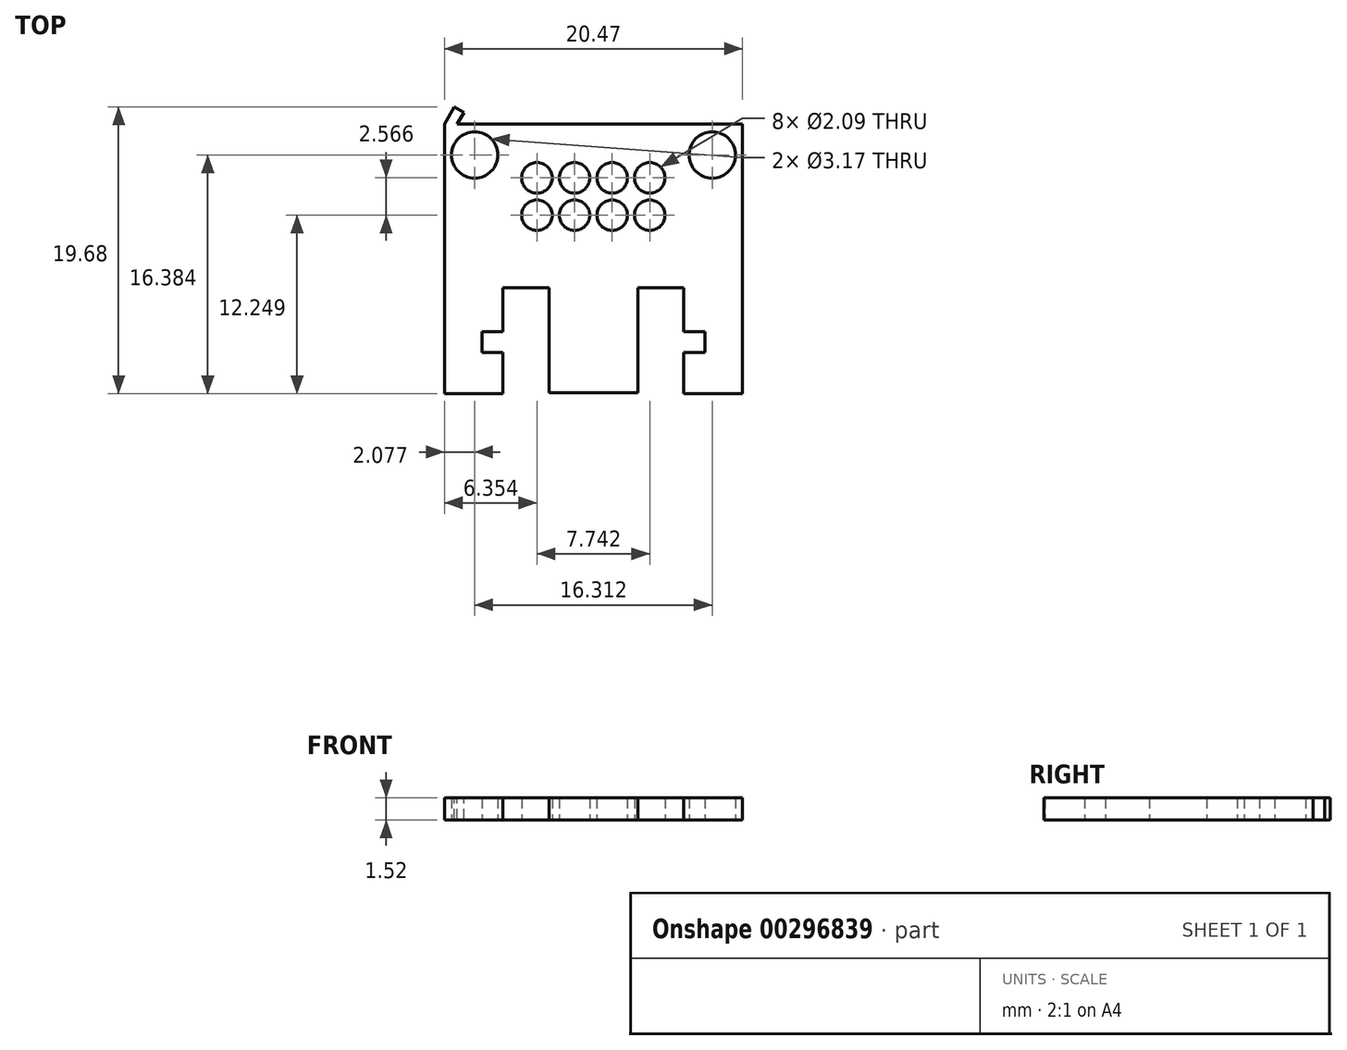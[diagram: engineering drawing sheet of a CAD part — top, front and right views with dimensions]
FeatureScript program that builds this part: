
annotation { "Feature Type Name" : "Feature", "Feature Type Description" : "" }
export const myFeature = defineFeature(function(context is Context, id is Id, definition is map)
    precondition{}
    {
        {
            var Q0;
            Q0=qCreatedBy(makeId("Top.planeOp"),FACE);
            var sketch = newSketch(context, id + "F0", { "sketchPlane" : qUnion([Q0])});
            skLineSegment(sketch, "E0.bottom", {"start": v(2.07, -0.14) * mm, "end": v(12.3, -0.14) * mm});
            skLineSegment(sketch, "E0.top", {"start": v(2.07, -18.64) * mm, "end": v(6.1, -18.64) * mm});
            skLineSegment(sketch, "E0.left", {"start": v(2.07, -0.14) * mm, "end": v(2.07, -18.64) * mm});
            skLineSegment(sketch, "E1", {"start": v(6.1, -18.64) * mm, "end": v(6.1, -15.83) * mm});
            skLineSegment(sketch, "E2", {"start": v(6.1, -15.83) * mm, "end": v(4.65, -15.83) * mm});
            skLineSegment(sketch, "E3", {"start": v(4.65, -15.83) * mm, "end": v(4.65, -14.4) * mm});
            skLineSegment(sketch, "E4", {"start": v(4.65, -14.4) * mm, "end": v(6.1, -14.4) * mm});
            skLineSegment(sketch, "E5", {"start": v(6.1, -14.4) * mm, "end": v(6.1, -11.39) * mm});
            skLineSegment(sketch, "E6", {"start": v(6.1, -11.39) * mm, "end": v(9.25, -11.39) * mm});
            skLineSegment(sketch, "E7", {"start": v(9.25, -11.39) * mm, "end": v(9.25, -18.58) * mm});
            skLineSegment(sketch, "E8", {"start": v(9.25, -18.58) * mm, "end": v(12.3, -18.58) * mm});
            skLineSegment(sketch, "E9", {"start": v(12.3, 0) * mm, "end": v(12.3, -18.58) * mm});
            skPoint(sketch, "E10.orphan", {"position": v(15.35, -18.58) * mm});
            skCircle(sketch, "E11", {"center": v(4.15, -2.26) * mm, "radius": 1.59 * mm});
            skSolve(sketch);
        }
        {
            var Q0;
            {var subQ0=sQuery(id+"F0.wireOp",EDGE,"E0.bottom");Q0=makeQuery(id+"F0.imprint","IMPRINT",FACE,{"disambiguationData":[TD([[makeQuery(id+"F0.imprint","IMPRINT",EDGE,{"derivedFrom":subQ0}),-1.0]])]});}
            extrude(context, id + "F1", {"entities" : qUnion([Q0]), "depth" : 1.52 * mm});
        }
        {
            var Q0;
            Q0=makeQuery(id+"F1.opExtrude","SWEPT_BODY",BODY,{"disambiguationData":[OSD([sQuery(id+"F0.wireOp",EDGE,"E0.bottom"),sQuery(id+"F0.wireOp",EDGE,"E0.top"),sQuery(id+"F0.wireOp",EDGE,"E0.left"),sQuery(id+"F0.wireOp",EDGE,"E1"),sQuery(id+"F0.wireOp",EDGE,"E2"),sQuery(id+"F0.wireOp",EDGE,"E3"),sQuery(id+"F0.wireOp",EDGE,"E4"),sQuery(id+"F0.wireOp",EDGE,"E5"),sQuery(id+"F0.wireOp",EDGE,"E6"),sQuery(id+"F0.wireOp",EDGE,"E7"),sQuery(id+"F0.wireOp",EDGE,"E8"),sQuery(id+"F0.wireOp",EDGE,"E9"),sQuery(id+"F0.wireOp",EDGE,"E11")])]});
            var Q1;
            Q1=makeQuery(id+"F1.opExtrude","SWEPT_FACE",FACE,{"disambiguationData":[OSD([sQuery(id+"F0.wireOp",EDGE,"E9")])]});
            mirror(context, id + "F2", {"operationType" : NewBodyOperationType.ADD, "entities" : qUnion([Q0]), "mirrorPlane" : qUnion([Q1])});
        }
        {
            var Q0;
            {var subQ0=makeQuery(id+"F1.opExtrude","CAP_FACE",FACE,{"disambiguationData":[OSD([sQuery(id+"F0.wireOp",EDGE,"E0.bottom"),sQuery(id+"F0.wireOp",EDGE,"E0.top"),sQuery(id+"F0.wireOp",EDGE,"E0.left"),sQuery(id+"F0.wireOp",EDGE,"E1"),sQuery(id+"F0.wireOp",EDGE,"E2"),sQuery(id+"F0.wireOp",EDGE,"E3"),sQuery(id+"F0.wireOp",EDGE,"E4"),sQuery(id+"F0.wireOp",EDGE,"E5"),sQuery(id+"F0.wireOp",EDGE,"E6"),sQuery(id+"F0.wireOp",EDGE,"E7"),sQuery(id+"F0.wireOp",EDGE,"E8"),sQuery(id+"F0.wireOp",EDGE,"E9"),sQuery(id+"F0.wireOp",EDGE,"E11")])],"isStart":true});Q0=makeQuery(id+"F2.boolean.opBoolean","MERGE",FACE,{"derivedFrom":[subQ0,makeQuery(id+"F2.opPattern","COPY",FACE,{"derivedFrom":subQ0,"instanceName":"1"})]});}
            var sketch = newSketch(context, id + "F3", { "sketchPlane" : qUnion([Q0])});
            skCircle(sketch, "E12", {"center": v(16.17, 3.82) * mm, "radius": 1.05 * mm});
            skLineSegment(sketch, "E13.bottom", {"start": v(16.17, 3.82) * mm, "end": v(8.42, 3.82) * mm, "construction": true});
            skLineSegment(sketch, "E13.top", {"start": v(16.17, 6.4) * mm, "end": v(8.42, 6.4) * mm, "construction": true});
            skLineSegment(sketch, "E13.left", {"start": v(16.17, 3.82) * mm, "end": v(16.17, 6.4) * mm, "construction": true});
            skLineSegment(sketch, "E13.right", {"start": v(8.42, 3.82) * mm, "end": v(8.42, 6.4) * mm, "construction": true});
            skCircle(sketch, "E14", {"center": v(13.58, 3.82) * mm, "radius": 1.05 * mm});
            skCircle(sketch, "E15", {"center": v(8.42, 3.82) * mm, "radius": 1.05 * mm});
            skCircle(sketch, "E16", {"center": v(8.42, 6.4) * mm, "radius": 1.05 * mm});
            skCircle(sketch, "E17", {"center": v(13.58, 6.4) * mm, "radius": 1.05 * mm});
            skCircle(sketch, "E18", {"center": v(16.17, 6.4) * mm, "radius": 1.05 * mm});
            skCircle(sketch, "E19", {"center": v(11, 3.82) * mm, "radius": 1.05 * mm});
            skCircle(sketch, "E20", {"center": v(11, 6.4) * mm, "radius": 1.05 * mm});
            skLineSegment(sketch, "E21", {"start": v(16.17, 3.82) * mm, "end": v(13.58, 3.82) * mm, "construction": true});
            skLineSegment(sketch, "E22", {"start": v(13.58, 3.82) * mm, "end": v(11, 3.82) * mm, "construction": true});
            skLineSegment(sketch, "E23", {"start": v(11, 3.82) * mm, "end": v(8.42, 3.82) * mm, "construction": true});
            skLineSegment(sketch, "E24", {"start": v(13.58, 3.82) * mm, "end": v(13.58, 6.4) * mm});
            skLineSegment(sketch, "E25", {"start": v(11, 3.82) * mm, "end": v(11, 6.4) * mm});
            skSolve(sketch);
        }
        {
            var Q0;
            Q0 = qSketchRegion(id + "F3", true);
            var Q1;
            Q1 = qConstructionFilter(qBodyType(qCreatedBy(id + "F3" ,EDGE), BodyType.WIRE), ConstructionObject.NO);
            extrude(context, id + "F4", {"entities" : qUnion([Q0]), "operationType" : NewBodyOperationType.REMOVE, "surfaceEntities" : qUnion([Q1]), "endBound" : BoundingType.THROUGH_ALL, "oppositeDirection" : true, "depth" : 25.4 * mm});
        }
        {
            var Q0;
            Q0=qCreatedBy(makeId("Front.planeOp"),FACE);
            var sketch = newSketch(context, id + "F5", { "sketchPlane" : qUnion([Q0])});
            skLineSegment(sketch, "E26", {"start": v(0, 0) * mm, "end": v(0, 24.29) * mm});
            skSolve(sketch);
        }
        {
            var Q0;
            {var subQ0=makeQuery(id+"F1.opExtrude","CAP_FACE",FACE,{"disambiguationData":[OSD([sQuery(id+"F0.wireOp",EDGE,"E0.bottom"),sQuery(id+"F0.wireOp",EDGE,"E0.top"),sQuery(id+"F0.wireOp",EDGE,"E0.left"),sQuery(id+"F0.wireOp",EDGE,"E1"),sQuery(id+"F0.wireOp",EDGE,"E2"),sQuery(id+"F0.wireOp",EDGE,"E3"),sQuery(id+"F0.wireOp",EDGE,"E4"),sQuery(id+"F0.wireOp",EDGE,"E5"),sQuery(id+"F0.wireOp",EDGE,"E6"),sQuery(id+"F0.wireOp",EDGE,"E7"),sQuery(id+"F0.wireOp",EDGE,"E8"),sQuery(id+"F0.wireOp",EDGE,"E9"),sQuery(id+"F0.wireOp",EDGE,"E11")])],"isStart":false});Q0=makeQuery(id+"F2.boolean.opBoolean","MERGE",FACE,{"derivedFrom":[subQ0,makeQuery(id+"F2.opPattern","COPY",FACE,{"derivedFrom":subQ0,"instanceName":"1"})]});}
            var sketch = newSketch(context, id + "F6", { "sketchPlane" : qUnion([Q0])});
            skLineSegment(sketch, "E27", {"start": v(2.07, -0.14) * mm, "end": v(2.75, 1.04) * mm});
            skLineSegment(sketch, "E28", {"start": v(2.75, 1.04) * mm, "end": v(3.4, 0.65) * mm});
            skLineSegment(sketch, "E29", {"start": v(3.4, 0.65) * mm, "end": v(2.95, -0.14) * mm});
            skSolve(sketch);
        }
        {
            var Q0;
            {var subQ0=sQuery(id+"F6.wireOp",EDGE,"E27");Q0=makeQuery(id+"F6.imprint","IMPRINT",FACE,{"disambiguationData":[TD([[makeQuery(id+"F6.imprint","IMPRINT",EDGE,{"derivedFrom":subQ0}),-1.0]])]});}
            var Q1;
            {var subQ0=makeQuery(id+"F1.opExtrude","CAP_FACE",FACE,{"disambiguationData":[OSD([sQuery(id+"F0.wireOp",EDGE,"E0.bottom"),sQuery(id+"F0.wireOp",EDGE,"E0.top"),sQuery(id+"F0.wireOp",EDGE,"E0.left"),sQuery(id+"F0.wireOp",EDGE,"E1"),sQuery(id+"F0.wireOp",EDGE,"E2"),sQuery(id+"F0.wireOp",EDGE,"E3"),sQuery(id+"F0.wireOp",EDGE,"E4"),sQuery(id+"F0.wireOp",EDGE,"E5"),sQuery(id+"F0.wireOp",EDGE,"E6"),sQuery(id+"F0.wireOp",EDGE,"E7"),sQuery(id+"F0.wireOp",EDGE,"E8"),sQuery(id+"F0.wireOp",EDGE,"E9"),sQuery(id+"F0.wireOp",EDGE,"E11")])],"isStart":true});Q1=makeQuery(id+"F2.boolean.opBoolean","MERGE",FACE,{"derivedFrom":[subQ0,makeQuery(id+"F2.opPattern","COPY",FACE,{"derivedFrom":subQ0,"instanceName":"1"})]});}
            extrude(context, id + "F7", {"entities" : qUnion([Q0]), "operationType" : NewBodyOperationType.ADD, "endBound" : BoundingType.UP_TO_SURFACE, "oppositeDirection" : true, "endBoundEntityFace" : qUnion([Q1]), "depth" : 25.4 * mm});
        }
    });
